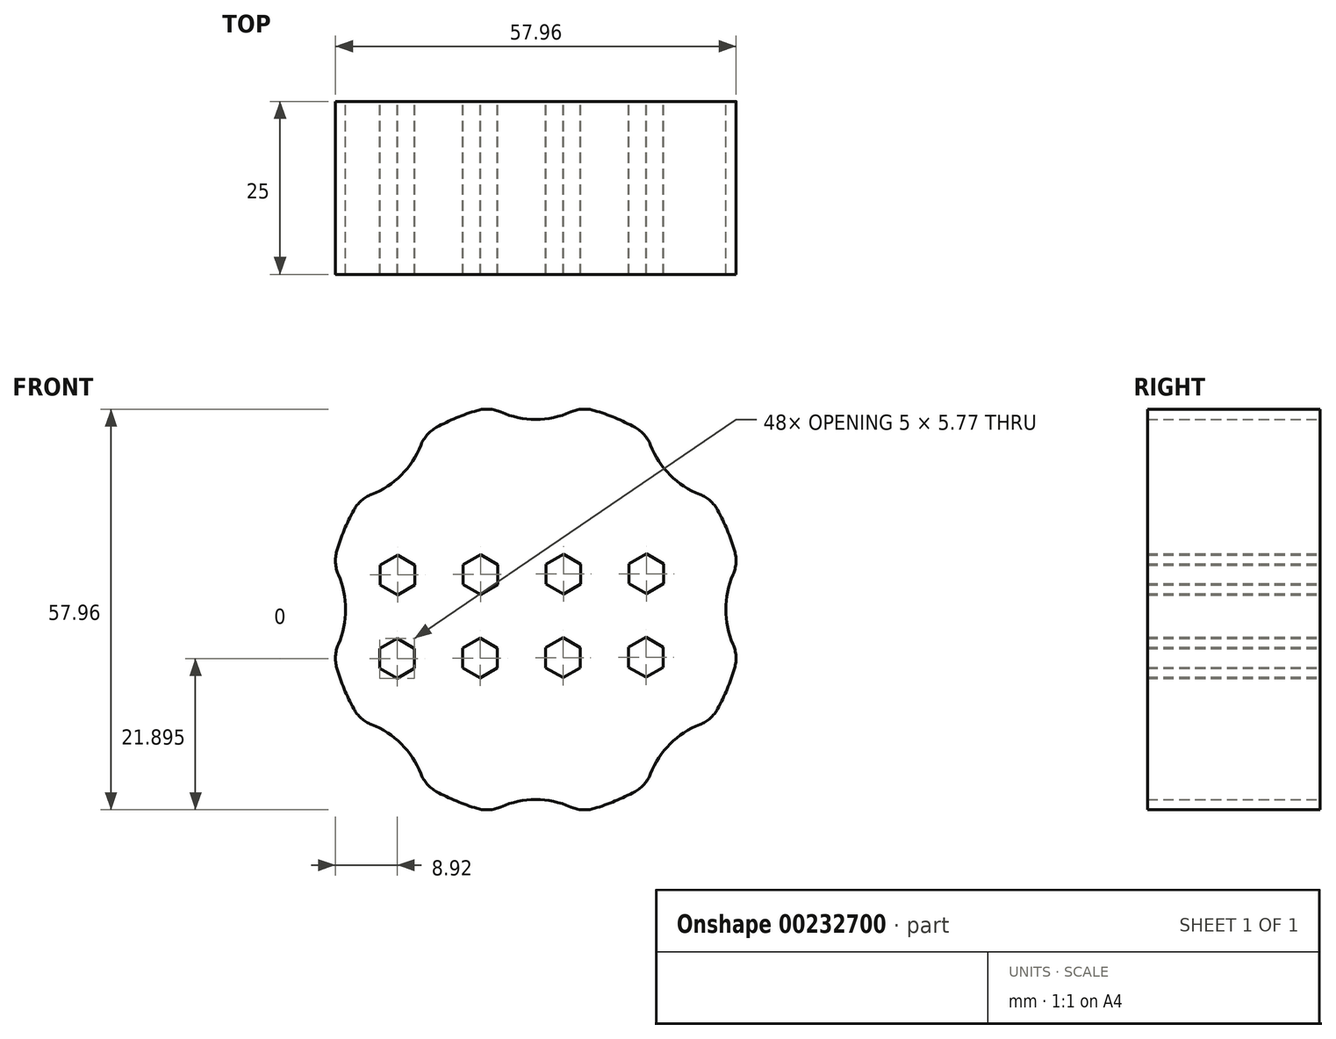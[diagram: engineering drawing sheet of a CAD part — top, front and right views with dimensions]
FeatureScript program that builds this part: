
annotation { "Feature Type Name" : "Feature", "Feature Type Description" : "" }
export const myFeature = defineFeature(function(context is Context, id is Id, definition is map)
    precondition{}
    {
        {
            var Q0;
            Q0=qCreatedBy(makeId("Front.planeOp"),FACE);
            var sketch = newSketch(context, id + "F0", { "sketchPlane" : qUnion([Q0])});
            skArc(sketch, "E0", {"start": v(-8.46, 28.78) * mm, "mid": v(-11.48, 27.72) * mm, "end": v(-14.37, 26.34) * mm});
            skArc(sketch, "E1", {"start": v(28.56, 5.04) * mm, "mid": v(27.5, 0) * mm, "end": v(28.56, -5.04) * mm});
            skPoint(sketch, "E1.centerSnap0", {"position": v(40, -1.22) * mm});
            skPoint(sketch, "E2.orphan", {"position": v(40, -9.76) * mm});
            skPoint(sketch, "E3.orphan", {"position": v(40, 7.33) * mm});
            skArc(sketch, "E4.1.0", {"start": v(16.63, 23.76) * mm, "mid": v(19.45, 19.45) * mm, "end": v(23.76, 16.63) * mm});
            skArc(sketch, "E4.2.0", {"start": v(-5.04, 28.56) * mm, "mid": v(0, 27.5) * mm, "end": v(5.04, 28.56) * mm});
            skArc(sketch, "E4.3.0", {"start": v(-23.76, 16.63) * mm, "mid": v(-19.45, 19.45) * mm, "end": v(-16.63, 23.76) * mm});
            skArc(sketch, "E4.4.0", {"start": v(-28.56, -5.04) * mm, "mid": v(-27.5, 0) * mm, "end": v(-28.56, 5.04) * mm});
            skArc(sketch, "E4.5.0", {"start": v(-16.63, -23.76) * mm, "mid": v(-19.45, -19.45) * mm, "end": v(-23.76, -16.63) * mm});
            skArc(sketch, "E4.6.0", {"start": v(5.04, -28.56) * mm, "mid": v(0, -27.5) * mm, "end": v(-5.04, -28.56) * mm});
            skArc(sketch, "E4.7.0", {"start": v(23.76, -16.63) * mm, "mid": v(19.45, -19.45) * mm, "end": v(16.63, -23.76) * mm});
            skArc(sketch, "E5.trimOffspring", {"start": v(14.37, 26.34) * mm, "mid": v(11.48, 27.72) * mm, "end": v(8.46, 28.78) * mm});
            skArc(sketch, "E6.trimOffspring", {"start": v(28.78, 8.46) * mm, "mid": v(27.72, 11.48) * mm, "end": v(26.34, 14.37) * mm});
            skArc(sketch, "E7.trimOffspring", {"start": v(26.34, -14.37) * mm, "mid": v(27.72, -11.48) * mm, "end": v(28.78, -8.46) * mm});
            skArc(sketch, "E8.trimOffspring", {"start": v(8.46, -28.78) * mm, "mid": v(11.48, -27.72) * mm, "end": v(14.37, -26.34) * mm});
            skArc(sketch, "E9.trimOffspring", {"start": v(-14.37, -26.34) * mm, "mid": v(-11.48, -27.72) * mm, "end": v(-8.46, -28.78) * mm});
            skArc(sketch, "E10.trimOffspring", {"start": v(-28.78, -8.46) * mm, "mid": v(-27.72, -11.48) * mm, "end": v(-26.34, -14.37) * mm});
            skArc(sketch, "E11.trimOffspring", {"start": v(-26.34, 14.37) * mm, "mid": v(-27.72, 11.48) * mm, "end": v(-28.78, 8.46) * mm});
            skPoint(sketch, "E12.visualSharp", {"position": v(16.15, 25.28) * mm});
            skArc(sketch, "E12.filletArc", {"start": v(16.63, 23.76) * mm, "mid": v(15.73, 25.25) * mm, "end": v(14.37, 26.34) * mm});
            skPoint(sketch, "E13.visualSharp", {"position": v(6.46, 29.3) * mm});
            skArc(sketch, "E13.filletArc", {"start": v(8.46, 28.78) * mm, "mid": v(6.73, 28.97) * mm, "end": v(5.04, 28.56) * mm});
            skPoint(sketch, "E14.visualSharp", {"position": v(-6.46, 29.3) * mm});
            skArc(sketch, "E14.filletArc", {"start": v(-5.04, 28.56) * mm, "mid": v(-6.73, 28.97) * mm, "end": v(-8.46, 28.78) * mm});
            skPoint(sketch, "E15.visualSharp", {"position": v(-16.15, 25.28) * mm});
            skArc(sketch, "E15.filletArc", {"start": v(-14.37, 26.34) * mm, "mid": v(-15.73, 25.25) * mm, "end": v(-16.63, 23.76) * mm});
            skPoint(sketch, "E16.visualSharp", {"position": v(-25.28, 16.15) * mm});
            skArc(sketch, "E16.filletArc", {"start": v(-23.76, 16.63) * mm, "mid": v(-25.25, 15.73) * mm, "end": v(-26.34, 14.37) * mm});
            skPoint(sketch, "E17.visualSharp", {"position": v(-29.3, 6.46) * mm});
            skArc(sketch, "E17.filletArc", {"start": v(-28.78, 8.46) * mm, "mid": v(-28.97, 6.73) * mm, "end": v(-28.56, 5.04) * mm});
            skPoint(sketch, "E18.visualSharp", {"position": v(-29.3, -6.46) * mm});
            skArc(sketch, "E18.filletArc", {"start": v(-28.56, -5.04) * mm, "mid": v(-28.97, -6.73) * mm, "end": v(-28.78, -8.46) * mm});
            skPoint(sketch, "E19.visualSharp", {"position": v(-25.28, -16.15) * mm});
            skArc(sketch, "E19.filletArc", {"start": v(-26.34, -14.37) * mm, "mid": v(-25.25, -15.73) * mm, "end": v(-23.76, -16.63) * mm});
            skPoint(sketch, "E20.visualSharp", {"position": v(-16.15, -25.28) * mm});
            skArc(sketch, "E20.filletArc", {"start": v(-16.63, -23.76) * mm, "mid": v(-15.73, -25.25) * mm, "end": v(-14.37, -26.34) * mm});
            skPoint(sketch, "E21.visualSharp", {"position": v(-6.46, -29.3) * mm});
            skArc(sketch, "E21.filletArc", {"start": v(-8.46, -28.78) * mm, "mid": v(-6.73, -28.97) * mm, "end": v(-5.04, -28.56) * mm});
            skPoint(sketch, "E22.visualSharp", {"position": v(6.46, -29.3) * mm});
            skArc(sketch, "E22.filletArc", {"start": v(5.04, -28.56) * mm, "mid": v(6.73, -28.97) * mm, "end": v(8.46, -28.78) * mm});
            skPoint(sketch, "E23.visualSharp", {"position": v(16.15, -25.28) * mm});
            skArc(sketch, "E23.filletArc", {"start": v(14.37, -26.34) * mm, "mid": v(15.73, -25.25) * mm, "end": v(16.63, -23.76) * mm});
            skPoint(sketch, "E24.visualSharp", {"position": v(25.28, -16.15) * mm});
            skArc(sketch, "E24.filletArc", {"start": v(23.76, -16.63) * mm, "mid": v(25.25, -15.73) * mm, "end": v(26.34, -14.37) * mm});
            skPoint(sketch, "E25.visualSharp", {"position": v(29.3, -6.46) * mm});
            skArc(sketch, "E25.filletArc", {"start": v(28.78, -8.46) * mm, "mid": v(28.97, -6.73) * mm, "end": v(28.56, -5.04) * mm});
            skPoint(sketch, "E26.visualSharp", {"position": v(29.3, 6.46) * mm});
            skArc(sketch, "E26.filletArc", {"start": v(28.56, 5.04) * mm, "mid": v(28.97, 6.73) * mm, "end": v(28.78, 8.46) * mm});
            skPoint(sketch, "E27.visualSharp", {"position": v(25.28, 16.15) * mm});
            skArc(sketch, "E27.filletArc", {"start": v(26.34, 14.37) * mm, "mid": v(25.25, 15.73) * mm, "end": v(23.76, 16.63) * mm});
            skLineSegment(sketch, "E28", {"start": v(-20, 27.26) * mm, "end": v(-20, -39.08) * mm, "construction": true});
            skLineSegment(sketch, "E29", {"start": v(-52.33, 0) * mm, "end": v(0, 0) * mm, "construction": true});
            skLineSegment(sketch, "E30", {"start": v(-23.17, 5) * mm, "end": v(-22.5, 5) * mm, "construction": true});
            skLineSegment(sketch, "E31.cCircle", {"start": v(-22.5, 5) * mm, "end": v(-22.5, 5) * mm});
            skLineSegment(sketch, "E31.0", {"start": v(-17.5, 3.56) * mm, "end": v(-20, 2.11) * mm});
            skLineSegment(sketch, "E31.1", {"start": v(-20, 2.11) * mm, "end": v(-22.5, 3.56) * mm});
            skLineSegment(sketch, "E31.2", {"start": v(-22.5, 3.56) * mm, "end": v(-22.5, 6.44) * mm});
            skLineSegment(sketch, "E31.3", {"start": v(-22.5, 6.44) * mm, "end": v(-20, 7.89) * mm});
            skLineSegment(sketch, "E31.4", {"start": v(-20, 7.89) * mm, "end": v(-17.5, 6.44) * mm});
            skLineSegment(sketch, "E31.5", {"start": v(-17.5, 6.44) * mm, "end": v(-17.5, 3.56) * mm});
            skPoint(sketch, "E31.0.midPoint", {"position": v(-18.75, 2.83) * mm});
            skLineSegment(sketch, "E32.trimOffspring", {"start": v(-17.5, 5) * mm, "end": v(-17.5, 5) * mm});
            skLineSegment(sketch, "E33.1.0.0", {"start": v(-10.5, 6.5) * mm, "end": v(-8, 7.94) * mm});
            skLineSegment(sketch, "E33.1.0.1", {"start": v(-10.5, 3.61) * mm, "end": v(-10.5, 6.5) * mm});
            skLineSegment(sketch, "E33.1.0.2", {"start": v(-8, 2.17) * mm, "end": v(-10.5, 3.61) * mm});
            skLineSegment(sketch, "E33.1.0.3", {"start": v(-5.5, 3.61) * mm, "end": v(-8, 2.17) * mm});
            skLineSegment(sketch, "E33.1.0.4", {"start": v(-5.5, 6.5) * mm, "end": v(-5.5, 3.61) * mm});
            skLineSegment(sketch, "E33.1.0.5", {"start": v(-8, 7.94) * mm, "end": v(-5.5, 6.5) * mm});
            skLineSegment(sketch, "E33.2.0.0", {"start": v(1.5, 6.56) * mm, "end": v(4, 8) * mm});
            skLineSegment(sketch, "E33.2.0.1", {"start": v(1.5, 3.67) * mm, "end": v(1.5, 6.56) * mm});
            skLineSegment(sketch, "E33.2.0.2", {"start": v(4, 2.23) * mm, "end": v(1.5, 3.67) * mm});
            skLineSegment(sketch, "E33.2.0.3", {"start": v(6.5, 3.67) * mm, "end": v(4, 2.23) * mm});
            skLineSegment(sketch, "E33.2.0.4", {"start": v(6.5, 6.56) * mm, "end": v(6.5, 3.67) * mm});
            skLineSegment(sketch, "E33.2.0.5", {"start": v(4, 8) * mm, "end": v(6.5, 6.56) * mm});
            skLineSegment(sketch, "E33.3.0.0", {"start": v(13.5, 6.61) * mm, "end": v(16, 8.06) * mm});
            skLineSegment(sketch, "E33.3.0.1", {"start": v(13.5, 3.73) * mm, "end": v(13.5, 6.61) * mm});
            skLineSegment(sketch, "E33.3.0.2", {"start": v(16, 2.28) * mm, "end": v(13.5, 3.73) * mm});
            skLineSegment(sketch, "E33.3.0.3", {"start": v(18.5, 3.73) * mm, "end": v(16, 2.28) * mm});
            skLineSegment(sketch, "E33.3.0.4", {"start": v(18.5, 6.61) * mm, "end": v(18.5, 3.73) * mm});
            skLineSegment(sketch, "E33.3.0.5", {"start": v(16, 8.06) * mm, "end": v(18.5, 6.61) * mm});
            skLineSegment(sketch, "E33.direction1", {"start": v(-22.5, 6.44) * mm, "end": v(-10.5, 6.5) * mm, "construction": true});
            skLineSegment(sketch, "E34", {"start": v(-25.45, -10) * mm, "end": v(-9.2, -10) * mm, "construction": true});
            skLineSegment(sketch, "E35", {"start": v(-23.17, 5) * mm, "end": v(-19, 5) * mm, "construction": true});
            skLineSegment(sketch, "E36.1.0.0", {"start": v(-20.06, -9.97) * mm, "end": v(-22.56, -8.53) * mm});
            skLineSegment(sketch, "E36.1.0.1", {"start": v(-22.56, -8.53) * mm, "end": v(-22.56, -5.64) * mm});
            skLineSegment(sketch, "E36.1.0.2", {"start": v(-22.56, -5.64) * mm, "end": v(-20.06, -4.2) * mm});
            skLineSegment(sketch, "E36.1.0.3", {"start": v(-20.06, -4.2) * mm, "end": v(-17.56, -5.64) * mm});
            skLineSegment(sketch, "E36.1.0.4", {"start": v(-17.56, -5.64) * mm, "end": v(-17.56, -8.53) * mm});
            skLineSegment(sketch, "E36.1.0.5", {"start": v(-17.56, -8.53) * mm, "end": v(-20.06, -9.97) * mm});
            skLineSegment(sketch, "E36.1.0.6", {"start": v(-10.56, -8.47) * mm, "end": v(-10.56, -5.59) * mm});
            skLineSegment(sketch, "E36.1.0.7", {"start": v(-8.06, -4.14) * mm, "end": v(-5.56, -5.59) * mm});
            skLineSegment(sketch, "E36.1.0.8", {"start": v(-5.56, -5.59) * mm, "end": v(-5.56, -8.47) * mm});
            skLineSegment(sketch, "E36.1.0.9", {"start": v(-5.56, -8.47) * mm, "end": v(-8.06, -9.92) * mm});
            skLineSegment(sketch, "E36.1.0.10", {"start": v(-8.06, -9.92) * mm, "end": v(-10.56, -8.47) * mm});
            skLineSegment(sketch, "E36.1.0.11", {"start": v(3.94, -9.86) * mm, "end": v(1.44, -8.42) * mm});
            skLineSegment(sketch, "E36.1.0.12", {"start": v(1.44, -8.42) * mm, "end": v(1.44, -5.53) * mm});
            skLineSegment(sketch, "E36.1.0.13", {"start": v(1.44, -5.53) * mm, "end": v(3.94, -4.09) * mm});
            skLineSegment(sketch, "E36.1.0.14", {"start": v(3.94, -4.09) * mm, "end": v(6.44, -5.53) * mm});
            skLineSegment(sketch, "E36.1.0.15", {"start": v(6.44, -5.53) * mm, "end": v(6.44, -8.42) * mm});
            skLineSegment(sketch, "E36.1.0.16", {"start": v(6.44, -8.42) * mm, "end": v(3.94, -9.86) * mm});
            skLineSegment(sketch, "E36.1.0.17", {"start": v(13.44, -5.47) * mm, "end": v(15.94, -4.03) * mm});
            skLineSegment(sketch, "E36.1.0.18", {"start": v(15.94, -4.03) * mm, "end": v(18.44, -5.47) * mm});
            skLineSegment(sketch, "E36.1.0.19", {"start": v(18.44, -5.47) * mm, "end": v(18.44, -8.36) * mm});
            skLineSegment(sketch, "E36.1.0.20", {"start": v(18.44, -8.36) * mm, "end": v(15.94, -9.8) * mm});
            skLineSegment(sketch, "E36.1.0.21", {"start": v(15.94, -9.8) * mm, "end": v(13.44, -8.36) * mm});
            skLineSegment(sketch, "E36.1.0.22", {"start": v(13.44, -8.36) * mm, "end": v(13.44, -5.47) * mm});
            skLineSegment(sketch, "E36.direction1", {"start": v(-22.5, 3.56) * mm, "end": v(-22.56, -8.53) * mm, "construction": true});
            skLineSegment(sketch, "E37", {"start": v(-10.56, -5.59) * mm, "end": v(-8.06, -4.14) * mm});
            skLineSegment(sketch, "E38", {"start": v(-20, 5) * mm, "end": v(-20, -7) * mm});
            skLineSegment(sketch, "E39", {"start": v(-20, -7) * mm, "end": v(-13.78, -7) * mm});
            skSolve(sketch);
        }
        {
            var Q0;
            Q0=makeQuery(id+"F0.imprint","IMPRINT",FACE,{"disambiguationData":[TD([[makeQuery(id+"F0.imprint","IMPRINT",EDGE,{"derivedFrom":sQuery(id+"F0.wireOp",EDGE,"E0")}),1.0]])]});
            extrude(context, id + "F1", {"entities" : qUnion([Q0]), "depth" : 25 * mm});
        }
    });
